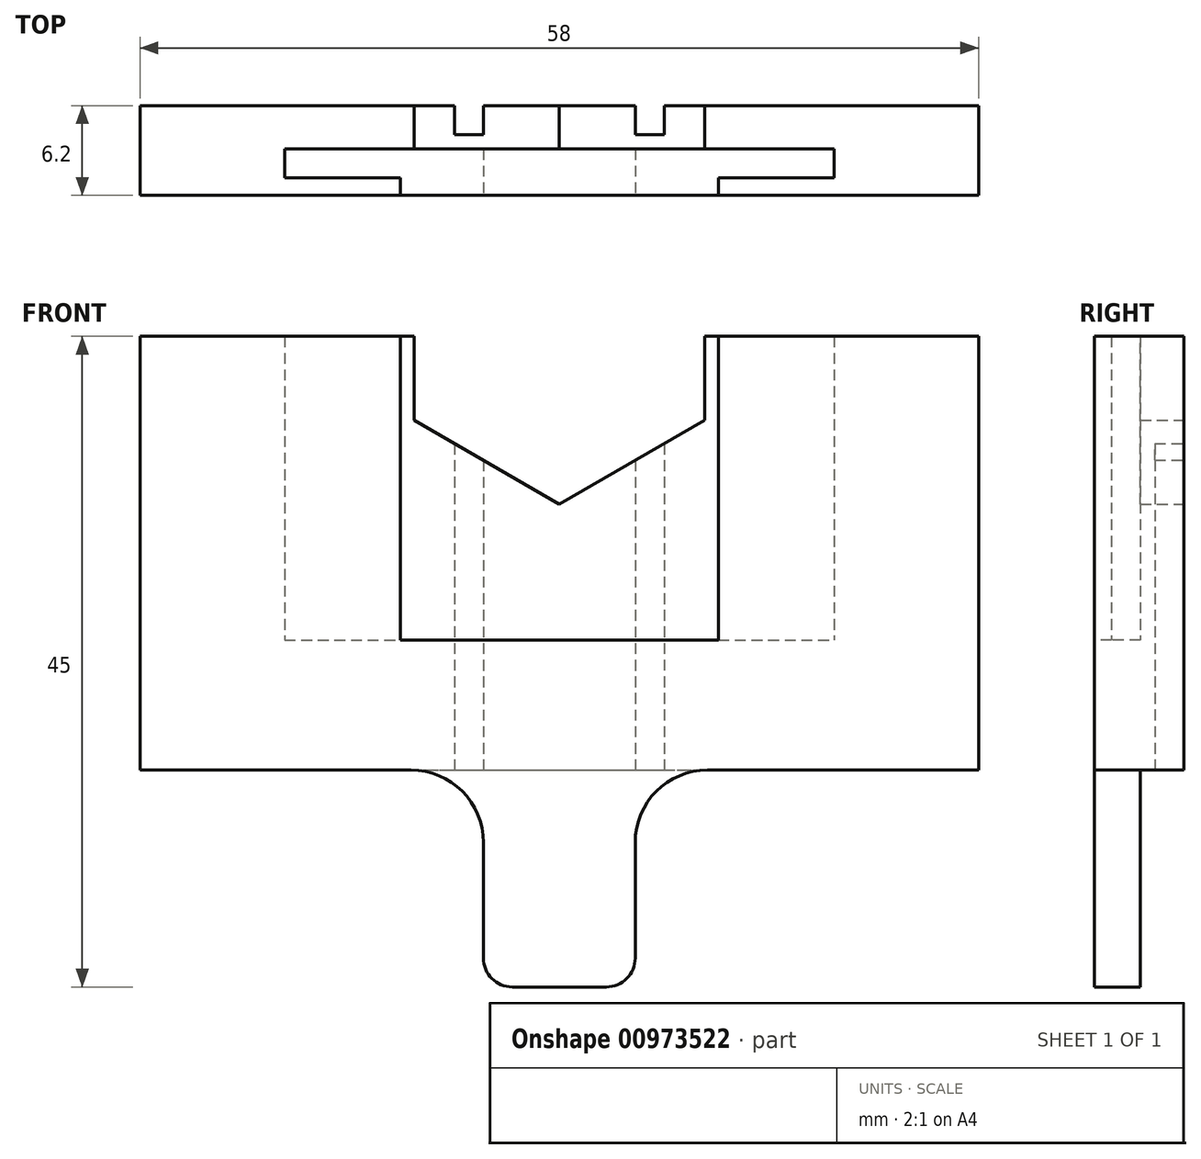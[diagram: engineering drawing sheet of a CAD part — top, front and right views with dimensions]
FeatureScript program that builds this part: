
annotation { "Feature Type Name" : "Feature", "Feature Type Description" : "" }
export const myFeature = defineFeature(function(context is Context, id is Id, definition is map)
    precondition{}
    {
        {
            var Q0;
            Q0=qCreatedBy(makeId("Top.planeOp"),FACE);
            var sketch = newSketch(context, id + "F0", { "sketchPlane" : qUnion([Q0])});
            skLineSegment(sketch, "E0.bottom", {"start": v(0, 0) * mm, "end": v(38, 0) * mm});
            skLineSegment(sketch, "E0.top", {"start": v(0, 1.2) * mm, "end": v(38, 1.2) * mm});
            skLineSegment(sketch, "E0.left", {"start": v(0, 0) * mm, "end": v(0, 1.2) * mm});
            skLineSegment(sketch, "E0.right", {"start": v(38, 0) * mm, "end": v(38, 1.2) * mm});
            skSolve(sketch);
        }
        {
            var Q0;
            Q0=qSketchRegion(id+"F0",true);
            extrude(context, id + "F1", {"entities" : qUnion([Q0]), "depth" : 20 * mm, "offsetDistance" : 25 * mm});
        }
        {
            var Q0;
            Q0=makeQuery(id+"F1.opExtrude","CAP_FACE",FACE,{"disambiguationData":[OSD([sQuery(id+"F0.wireOp",EDGE,"E0.bottom"),sQuery(id+"F0.wireOp",EDGE,"E0.top"),sQuery(id+"F0.wireOp",EDGE,"E0.left"),sQuery(id+"F0.wireOp",EDGE,"E0.right")])],"isStart":false});
            var sketch = newSketch(context, id + "F2", { "sketchPlane" : qUnion([Q0])});
            skLineSegment(sketch, "E1", {"start": v(8, 1.2) * mm, "end": v(8, 0) * mm});
            skLineSegment(sketch, "E2", {"start": v(30, 1.2) * mm, "end": v(30, 0) * mm});
            skLineSegment(sketch, "E3", {"start": v(8, 0) * mm, "end": v(30, 0) * mm});
            skLineSegment(sketch, "E4", {"start": v(30, 1.2) * mm, "end": v(8, 1.2) * mm});
            skSolve(sketch);
        }
        {
            var Q0;
            {var subQ1=sQuery(id+"F0.wireOp",EDGE,"E0.left");var subQ3=sQuery(id+"F0.wireOp",EDGE,"E0.bottom");Q0=makeQuery(id+"F7oCdRpcySzvxNv_1.boolean.opBoolean","SPLIT",FACE,{"disambiguationData":[TD([makeQuery(id+"F1.opExtrude","SWEPT_FACE",FACE,{"disambiguationData":[OSD([subQ1])]})])],"derivedFrom":makeQuery(id+"F1.opExtrude","SWEPT_FACE",FACE,{"disambiguationData":[OSD([subQ3])]})});}
            var sketch = newSketch(context, id + "F3", { "sketchPlane" : qUnion([Q0])});
            skLineSegment(sketch, "E5.bottom", {"start": v(0, 0) * mm, "end": v(-10, 0) * mm});
            skLineSegment(sketch, "E5.top", {"start": v(0, 20) * mm, "end": v(-10, 20) * mm});
            skLineSegment(sketch, "E5.left", {"start": v(0, 0) * mm, "end": v(0, 20) * mm});
            skLineSegment(sketch, "E5.right", {"start": v(-10, 0) * mm, "end": v(-10, 20) * mm});
            skSolve(sketch);
        }
        {
            var Q0;
            Q0=makeQuery(id+"F3.imprint","IMPRINT",FACE,{"disambiguationData":[TD([[makeQuery(id+"F3.imprint","IMPRINT",EDGE,{"derivedFrom":sQuery(id+"F3.wireOp",EDGE,"E5.bottom")}),-1.0]])]});
            extrude(context, id + "F4", {"entities" : qUnion([Q0]), "operationType" : NewBodyOperationType.ADD, "oppositeDirection" : true, "depth" : 3.2 * mm, "offsetDistance" : 25 * mm});
        }
        {
            var Q0;
            Q0=makeQuery(id+"F4.boolean.opBoolean","MERGE",FACE,{"derivedFrom":[makeQuery(id+"F1.opExtrude","SWEPT_FACE",FACE,{"disambiguationData":[OSD([sQuery(id+"F0.wireOp",EDGE,"E0.bottom")])]}),makeQuery(id+"F4.opExtrude","CAP_FACE",FACE,{"disambiguationData":[OSD([sQuery(id+"F3.wireOp",EDGE,"E5.bottom"),sQuery(id+"F3.wireOp",EDGE,"E5.top"),sQuery(id+"F3.wireOp",EDGE,"E5.left"),sQuery(id+"F3.wireOp",EDGE,"E5.right")])],"isStart":true})]});
            var sketch = newSketch(context, id + "F5", { "sketchPlane" : qUnion([Q0])});
            skLineSegment(sketch, "E6.bottom", {"start": v(38, 0) * mm, "end": v(48, 0) * mm});
            skLineSegment(sketch, "E6.top", {"start": v(38, 20) * mm, "end": v(48, 20) * mm});
            skLineSegment(sketch, "E6.left", {"start": v(38, 0) * mm, "end": v(38, 20) * mm});
            skLineSegment(sketch, "E6.right", {"start": v(48, 0) * mm, "end": v(48, 20) * mm});
            skSolve(sketch);
        }
        {
            var Q0;
            Q0=makeQuery(id+"F5.imprint","IMPRINT",FACE,{"disambiguationData":[TD([[makeQuery(id+"F5.imprint","IMPRINT",EDGE,{"derivedFrom":sQuery(id+"F5.wireOp",EDGE,"E6.bottom")}),1.0]])]});
            extrude(context, id + "F6", {"entities" : qUnion([Q0]), "operationType" : NewBodyOperationType.ADD, "oppositeDirection" : true, "depth" : 3.2 * mm, "offsetDistance" : 25 * mm});
        }
        {
            var Q0;
            Q0=makeQuery(id+"F6.boolean.opBoolean","MERGE",FACE,{"derivedFrom":[makeQuery(id+"F4.boolean.opBoolean","MERGE",FACE,{"derivedFrom":[makeQuery(id+"F1.opExtrude","CAP_FACE",FACE,{"disambiguationData":[OSD([sQuery(id+"F0.wireOp",EDGE,"E0.bottom"),sQuery(id+"F0.wireOp",EDGE,"E0.top"),sQuery(id+"F0.wireOp",EDGE,"E0.left"),sQuery(id+"F0.wireOp",EDGE,"E0.right")])],"isStart":true}),makeQuery(id+"F4.opExtrude","SWEPT_FACE",FACE,{"disambiguationData":[OSD([sQuery(id+"F3.wireOp",EDGE,"E5.bottom")])]})]}),makeQuery(id+"F6.opExtrude","SWEPT_FACE",FACE,{"disambiguationData":[OSD([sQuery(id+"F5.wireOp",EDGE,"E6.bottom")])]})]});
            var sketch = newSketch(context, id + "F7", { "sketchPlane" : qUnion([Q0])});
            skLineSegment(sketch, "E7.bottom", {"start": v(48, 0) * mm, "end": v(-10, 0) * mm});
            skLineSegment(sketch, "E7.top", {"start": v(48, -3.2) * mm, "end": v(-10, -3.2) * mm});
            skLineSegment(sketch, "E7.left", {"start": v(48, 0) * mm, "end": v(48, -3.2) * mm});
            skLineSegment(sketch, "E7.right", {"start": v(-10, 0) * mm, "end": v(-10, -3.2) * mm});
            skSolve(sketch);
        }
        {
            var Q0;
            Q0=makeQuery(id+"F7.imprint","IMPRINT",FACE,{"disambiguationData":[TD([[makeQuery(id+"F7.imprint","IMPRINT",EDGE,{"derivedFrom":makeQuery(id+"F1.opExtrude","CAP_EDGE",EDGE,{"disambiguationData":[OSD([sQuery(id+"F0.wireOp",EDGE,"E0.top")])],"isStart":true})}),-1.0]])]});
            var Q1;
            Q1=makeQuery(id+"F7.imprint","IMPRINT",FACE,{"disambiguationData":[TD([[makeQuery(id+"F7.imprint","IMPRINT",EDGE,{"derivedFrom":sQuery(id+"F7.wireOp",EDGE,"E7.bottom")}),-1.0]])]});
            extrude(context, id + "F8", {"entities" : qUnion([Q0, Q1]), "operationType" : NewBodyOperationType.ADD, "depth" : 10 * mm, "offsetDistance" : 25 * mm});
        }
        {
            var Q0;
            Q0=makeQuery(id+"F2.imprint","IMPRINT",FACE,{"disambiguationData":[TD([[makeQuery(id+"F2.imprint","IMPRINT",EDGE,{"derivedFrom":sQuery(id+"F2.wireOp",EDGE,"E1")}),1.0]])]});
            extrude(context, id + "F9", {"entities" : qUnion([Q0]), "operationType" : NewBodyOperationType.REMOVE, "oppositeDirection" : true, "depth" : 20 * mm, "offsetDistance" : 25 * mm});
        }
        {
            var Q0;
            Q0=makeQuery(id+"F8.boolean.opBoolean","MERGE",FACE,{"derivedFrom":[makeQuery(id+"F6.opExtrude","SWEPT_FACE",FACE,{"disambiguationData":[OSD([sQuery(id+"F5.wireOp",EDGE,"E6.right")])]}),makeQuery(id+"F8.opExtrude","SWEPT_FACE",FACE,{"disambiguationData":[OSD([sQuery(id+"F7.wireOp",EDGE,"E7.left")])]})]});
            var sketch = newSketch(context, id + "F10", { "sketchPlane" : qUnion([Q0])});
            skLineSegment(sketch, "E8.bottom", {"start": v(3.2, -10) * mm, "end": v(6.2, -10) * mm});
            skLineSegment(sketch, "E8.top", {"start": v(3.2, 20) * mm, "end": v(6.2, 20) * mm});
            skLineSegment(sketch, "E8.left", {"start": v(3.2, -10) * mm, "end": v(3.2, 20) * mm});
            skLineSegment(sketch, "E8.right", {"start": v(6.2, -10) * mm, "end": v(6.2, 20) * mm});
            skSolve(sketch);
        }
        {
            var Q0;
            Q0=makeQuery(id+"F10.imprint","IMPRINT",FACE,{"disambiguationData":[TD([[makeQuery(id+"F10.imprint","IMPRINT",EDGE,{"derivedFrom":sQuery(id+"F10.wireOp",EDGE,"E8.bottom")}),1.0]])]});
            extrude(context, id + "F11", {"entities" : qUnion([Q0]), "oppositeDirection" : true, "depth" : 58 * mm, "offsetDistance" : 25 * mm});
        }
        {
            var Q0;
            Q0=makeQuery(id+"F11.opExtrude","SWEPT_FACE",FACE,{"disambiguationData":[OSD([sQuery(id+"F10.wireOp",EDGE,"E8.right")])]});
            var sketch = newSketch(context, id + "F12", { "sketchPlane" : qUnion([Q0])});
            skLineSegment(sketch, "E9", {"start": v(-29.06, 16.2) * mm, "end": v(-8.95, 23.8) * mm, "construction": true});
            skLineSegment(sketch, "E10", {"start": v(-29.05, 23.78) * mm, "end": v(-8.95, 16.22) * mm, "construction": true});
            skCircle(sketch, "E11.cCircle", {"center": v(-19, 20) * mm, "radius": 10.05 * mm, "construction": true});
            skPoint(sketch, "E11.cCircle.centerSnap0", {"position": v(-19, 20) * mm});
            skLineSegment(sketch, "E11.0", {"start": v(-29.05, 14.2) * mm, "end": v(-29.05, 25.8) * mm});
            skLineSegment(sketch, "E11.1", {"start": v(-29.05, 25.8) * mm, "end": v(-19, 31.6) * mm});
            skLineSegment(sketch, "E11.2", {"start": v(-19, 31.6) * mm, "end": v(-8.95, 25.8) * mm});
            skLineSegment(sketch, "E11.3", {"start": v(-8.95, 25.8) * mm, "end": v(-8.95, 14.2) * mm});
            skLineSegment(sketch, "E11.4", {"start": v(-8.95, 14.2) * mm, "end": v(-19, 8.4) * mm});
            skLineSegment(sketch, "E11.5", {"start": v(-19, 8.4) * mm, "end": v(-29.05, 14.2) * mm});
            skPoint(sketch, "E11.0.midPoint", {"position": v(-29.05, 20) * mm});
            skLineSegment(sketch, "E12", {"start": v(-8.95, 20) * mm, "end": v(-29.05, 20) * mm});
            skSolve(sketch);
        }
        {
            var Q0;
            {var subQ1=sQuery(id+"F12.wireOp",EDGE,"E11.4");Q0=makeQuery(id+"F12.imprint","IMPRINT",FACE,{"disambiguationData":[TD([[makeQuery(id+"F12.imprint","IMPRINT",EDGE,{"derivedFrom":subQ1}),-1.0]])]});}
            extrude(context, id + "F13", {"entities" : qUnion([Q0]), "operationType" : NewBodyOperationType.REMOVE, "endBound" : BoundingType.THROUGH_ALL, "oppositeDirection" : true, "depth" : 25 * mm, "offsetDistance" : 25 * mm});
        }
        {
            var Q0;
            Q0=makeQuery(id+"F11.opExtrude","SWEPT_FACE",FACE,{"disambiguationData":[OSD([sQuery(id+"F10.wireOp",EDGE,"E8.right")])]});
            var sketch = newSketch(context, id + "F14", { "sketchPlane" : qUnion([Q0])});
            skLineSegment(sketch, "E13", {"start": v(-26.25, 12.35) * mm, "end": v(-26.25, -16.15) * mm});
            skLineSegment(sketch, "E14", {"start": v(-11.75, 12.35) * mm, "end": v(-11.75, -16.7) * mm});
            skLineSegment(sketch, "E15", {"start": v(-24.25, 11.2) * mm, "end": v(-24.25, -16.27) * mm});
            skLineSegment(sketch, "E16", {"start": v(-13.75, 11.2) * mm, "end": v(-13.75, -16.1) * mm});
            skLineSegment(sketch, "E17", {"start": v(-24.25, -16.27) * mm, "end": v(-26.25, -16.15) * mm});
            skLineSegment(sketch, "E18", {"start": v(-13.75, -16.1) * mm, "end": v(-11.75, -16.7) * mm});
            skLineSegment(sketch, "E19", {"start": v(-24.25, -16.27) * mm, "end": v(-24.25, 11.2) * mm});
            skLineSegment(sketch, "E20", {"start": v(-26.25, 12.35) * mm, "end": v(-24.25, 11.2) * mm});
            skLineSegment(sketch, "E21", {"start": v(-26.25, 12.35) * mm, "end": v(-26.25, 13.17) * mm});
            skLineSegment(sketch, "E22", {"start": v(-26.25, 13.17) * mm, "end": v(-24.25, 13.17) * mm});
            skLineSegment(sketch, "E23", {"start": v(-24.25, 13.17) * mm, "end": v(-24.25, 11.2) * mm});
            skLineSegment(sketch, "E24", {"start": v(-13.75, 11.2) * mm, "end": v(-13.75, 12.88) * mm});
            skLineSegment(sketch, "E25", {"start": v(-13.75, 12.88) * mm, "end": v(-11.75, 12.58) * mm});
            skLineSegment(sketch, "E26", {"start": v(-11.75, 12.58) * mm, "end": v(-11.75, 12.35) * mm});
            skSolve(sketch);
        }
        {
            var Q0;
            Q0 = qSketchRegion(id + "F14", true);
            var Q1;
            {var subQ0=sQuery(id+"F14.wireOp",EDGE,"E13");var subQ1=makeQuery(id+"FcrtRvxJJIUddea_3.boolean.opBoolean","COPY",EDGE,{"derivedFrom":makeQuery(id+"FcrtRvxJJIUddea_3.opExtrude","CAP_EDGE",EDGE,{"disambiguationData":[OSD([sQuery(id+"FnyvmD6cRaVMi6d_3.wireOp",EDGE,"K94ibmXW-4yZ4-C50m-2syX-n6lYhoJBMCHx"),sQuery(id+"FnyvmD6cRaVMi6d_3.wireOp",EDGE,"lfh4j7G8-Y9ge-c0dc-HeIp-v5p37tLxIn1i")])],"isStart":true})});var subQ2=makeQuery(id+"F14.imprint","INTERSECT",VERTEX,{"derivedFrom":[subQ1,subQ0]});Q1=makeQuery(id+"F14.imprint","IMPRINT",FACE,{"disambiguationData":[TD([[makeQuery(id+"F14.imprint","IMPRINT",EDGE,{"disambiguationData":[TD([[subQ2,-1.0]])],"derivedFrom":subQ0}),1.0]])]});}
            var Q2;
            {var subQ0=sQuery(id+"F14.wireOp",EDGE,"E14");var subQ1=makeQuery(id+"FcrtRvxJJIUddea_3.boolean.opBoolean","COPY",EDGE,{"derivedFrom":makeQuery(id+"FcrtRvxJJIUddea_3.opExtrude","CAP_EDGE",EDGE,{"disambiguationData":[OSD([sQuery(id+"FnyvmD6cRaVMi6d_3.wireOp",EDGE,"VxK511Qp-mGPE-xUyt-g3Jn-2VVsL44pV6Ht")])],"isStart":true})});var subQ2=makeQuery(id+"F14.imprint","INTERSECT",VERTEX,{"derivedFrom":[subQ1,subQ0]});Q2=makeQuery(id+"F14.imprint","IMPRINT",FACE,{"disambiguationData":[TD([[makeQuery(id+"F14.imprint","IMPRINT",EDGE,{"disambiguationData":[TD([[subQ2,-1.0]])],"derivedFrom":subQ1}),1.0]])]});}
            extrude(context, id + "F15", {"entities" : qUnion([Q0, Q1, Q2]), "operationType" : NewBodyOperationType.REMOVE, "oppositeDirection" : true, "depth" : 2 * mm, "offsetDistance" : 25 * mm});
        }
        {
            var Q0;
            Q0=makeQuery(id+"F11.opExtrude","SWEPT_FACE",FACE,{"disambiguationData":[OSD([sQuery(id+"F10.wireOp",EDGE,"E8.bottom")])]});
            var sketch = newSketch(context, id + "F16", { "sketchPlane" : qUnion([Q0])});
            skLineSegment(sketch, "E27.bottom", {"start": v(13.75, -3.2) * mm, "end": v(24.25, -3.2) * mm});
            skLineSegment(sketch, "E27.top", {"start": v(13.75, 0) * mm, "end": v(24.25, 0) * mm});
            skLineSegment(sketch, "E27.left", {"start": v(13.75, -3.2) * mm, "end": v(13.75, 0) * mm});
            skLineSegment(sketch, "E27.right", {"start": v(24.25, -3.2) * mm, "end": v(24.25, 0) * mm});
            skSolve(sketch);
        }
        {
            var Q0;
            Q0=makeQuery(id+"F16.imprint","IMPRINT",FACE,{"disambiguationData":[TD([[makeQuery(id+"F16.imprint","IMPRINT",EDGE,{"derivedFrom":sQuery(id+"F16.wireOp",EDGE,"E27.bottom")}),1.0]])]});
            extrude(context, id + "F17", {"entities" : qUnion([Q0]), "operationType" : NewBodyOperationType.ADD, "depth" : 15 * mm, "offsetDistance" : 25 * mm});
        }
        {
            var Q0;
            Q0=makeQuery(id+"F17.opExtrude","CAP_EDGE",EDGE,{"disambiguationData":[OSD([sQuery(id+"F16.wireOp",EDGE,"E27.right")])],"isStart":true});
            var Q1;
            Q1=makeQuery(id+"F17.opExtrude","CAP_EDGE",EDGE,{"disambiguationData":[OSD([sQuery(id+"F16.wireOp",EDGE,"E27.left")])],"isStart":true});
            fillet(context, id + "F18", {"entities" : qUnion([Q0, Q1]), "tangentPropagation" : true, "radius" : 5 * mm, "defaultsChanged" : false, "vertexSettings" : [], "allowEdgeOverflow" : false});
        }
        {
            var Q0;
            Q0=makeQuery(id+"F17.opExtrude","CAP_EDGE",EDGE,{"disambiguationData":[OSD([sQuery(id+"F16.wireOp",EDGE,"E27.right")])],"isStart":false});
            var Q1;
            Q1=makeQuery(id+"F17.opExtrude","CAP_EDGE",EDGE,{"disambiguationData":[OSD([sQuery(id+"F16.wireOp",EDGE,"E27.left")])],"isStart":false});
            fillet(context, id + "F19", {"entities" : qUnion([Q0, Q1]), "tangentPropagation" : true, "radius" : 2 * mm, "defaultsChanged" : true, "vertexSettings" : [], "allowEdgeOverflow" : false});
        }
        {
            var Q0;
            Q0=makeQuery(id+"F9.boolean.opBoolean","MERGE",FACE,{"derivedFrom":[makeQuery(id+"F8.opExtrude","CAP_FACE",FACE,{"disambiguationData":[OSD([sQuery(id+"F7.wireOp",EDGE,"E7.bottom"),sQuery(id+"F7.wireOp",EDGE,"E7.top"),sQuery(id+"F7.wireOp",EDGE,"E7.left"),sQuery(id+"F7.wireOp",EDGE,"E7.right")])],"isStart":true})],"fromTools":[makeQuery(id+"F9.opExtrude","CAP_FACE",FACE,{"disambiguationData":[OSD([sQuery(id+"F2.wireOp",EDGE,"E1"),sQuery(id+"F2.wireOp",EDGE,"E2"),sQuery(id+"F2.wireOp",EDGE,"E3"),sQuery(id+"F2.wireOp",EDGE,"E4")])],"isStart":false})]});
            extrude(context, id + "F20", {"entities" : qUnion([Q0]), "operationType" : NewBodyOperationType.REMOVE, "oppositeDirection" : true, "depth" : 1 * mm, "offsetDistance" : 25 * mm});
        }
    });
